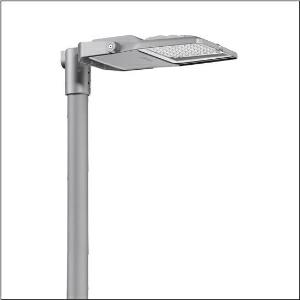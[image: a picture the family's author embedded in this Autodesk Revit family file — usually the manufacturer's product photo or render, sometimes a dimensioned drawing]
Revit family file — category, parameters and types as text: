
# Revit family: floodlight_fl_21_iq_mini___pl33t_5xa7771b4f3a_1cb2
name_source: partatom
category: Lighting Fixtures
units: mm (PartAtom-declared; Revit-internal decimal feet)

## family parameters
Cut with Voids When Loaded = No
Host = Face
Light Source = No
Part Type = Normal
Room Calculation Point = No
Round Connector Dimension = Use Diameter
Shared = No

## types (1)
- --- (1 x LED, 6420 lm, 45.5 W, 4000K)
    Apparent Load = 46 VA
    CIE Flux Codes = 26 75 99 100 100
    Color Rendering = 70
    Color Temperature = 4000K
    Default Elevation = 1800 mm
    Description = Floodlight FL 21 iQ mini, floodlight, primary light control with lens, of PMMA, primary optical cover: protective disc, of toughened safety glass, transparent, light distribution: PL33T, light emission: direct distribution, installation type: surface-mounted, LED, High Power LED, rated luminous flux: 6.420lm, luminous efficacy: 141lm/W, light colour: 740, colour temperature: 4000K, control: Auto-Match, Temp-Guard, Lumen-Switch, Night-Set, Smart-Wire, Light-Fading, Desk-Remote (wireless, voltage-free reading and setting of iQ features in the workshop via application-optimized NFC function/RFID function), optimised constant luminous flux control (CLO 2.0), with terminal, 6-pole, mains connection: 220..240V, AC, 50/60Hz, start of lifetime: 46W, end of service life: 48W, reduction: 22W, luminaire housing, of diecast aluminium, powder-coated, Siteco® metallic grey (DB 702S), corrosivity category C5 mid according to DIN EN ISO 12944, sealing non-destructively replaceable, please order mast flange separately, mast bracket, of steel, galvanised, powder-coated, Siteco® metallic grey (DB 702S), protection rating (complete): IP66, insulation class (complete): insulation class II (safety insulation), certification: CE, ENEC, VDE, protection symbol: D, impact resistance: IK08, permissible operating ambient temperature: -40..+40°C, permissible operating ambient temperature for outdoor applications: -40..+50°C, standard: DIN EN 12944, LABS conformity tested according to VDMA 24364:2018-05, packaging unit: 1 piece

Light Distribution: PL33T
    Height = 70 mm
    Lamp = 1 x LED
    Lamp Light Flux = 6420 lm
    Lamp Power = 45.5 W
    Lamp count = 1
    Length = 485 mm
    Luminous efficacy = 141 lm/W
    Manufacturer = Siteco
    ModVariant = No
    Model = 5XA7771B4F3A
    Number of Poles = 1
    OnlyDefault = Yes
    Power Factor = 1
    Product Name = Floodlight FL 21 iQ mini | PL33T
    Product group = floodlight | pylon annexe
    ProductGroupID = 6200
    Protection Class = Protection class II
    Protection Degree = IP 66
    RLX_Detail_Level = 1
    RLX_Emergency_Light_Flux = 0 lm
    RLX_Emergency_Type = 0
    RLX_Emergency_Type_DB = No
    RlxData = <blob elided: 101085 chars, md5=ca4024ba>
    Socket = socket
    Standby Power = 0 W
    System Light Flux = 6420 lm
    System Power = 46 W
    Type Comments = factory setting: luminous flux: 100 % | dim-lin: 254 | 463 mA
    Type Image = l_1007125.jpg
    URL = http://relux.com
    VarID = @adj_100333
    Voltage = 0 V
    Weight = 0.00 kg
    Width = 337 mm

## geometry (parser evidence)
native form markers: Blend x4, Sweep x12
no freeform markers — native parametric forms only
